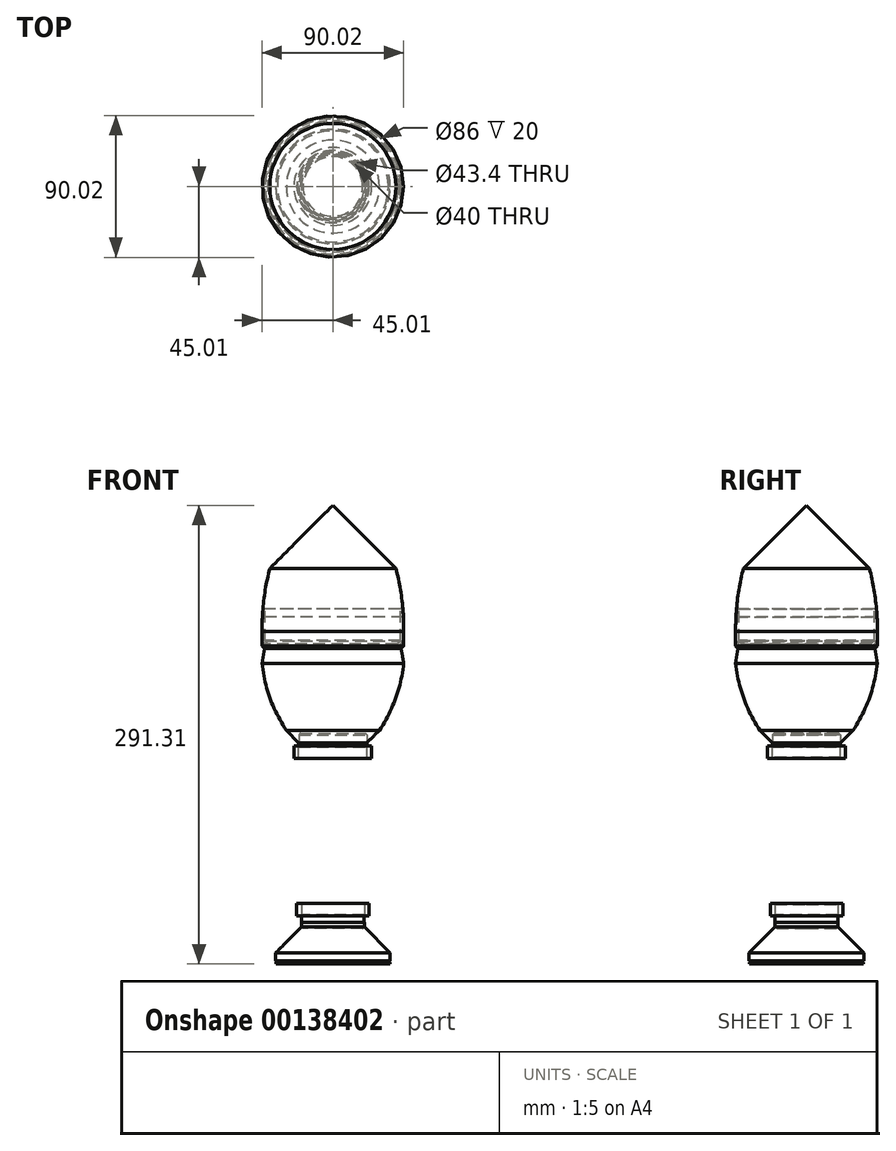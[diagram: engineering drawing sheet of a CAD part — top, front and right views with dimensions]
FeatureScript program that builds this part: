
annotation { "Feature Type Name" : "Feature", "Feature Type Description" : "" }
export const myFeature = defineFeature(function(context is Context, id is Id, definition is map)
    precondition{}
    {
        {
            var Q0;
            Q0=qCreatedBy(makeId("Front.planeOp"),FACE);
            var sketch = newSketch(context, id + "F0", { "sketchPlane" : qUnion([Q0])});
            skLineSegment(sketch, "E0", {"start": v(0, 155.81) * mm, "end": v(0, -136.19) * mm});
            skSolve(sketch);
        }
        {
            var Q0;
            Q0=qCreatedBy(makeId("Front.planeOp"),FACE);
            var sketch = newSketch(context, id + "F1", { "sketchPlane" : qUnion([Q0])});
            skLineSegment(sketch, "E1", {"start": v(0, 152.81) * mm, "end": v(40, 112.81) * mm});
            skPoint(sketch, "E2", {"position": v(44, 112.81) * mm});
            skLineSegment(sketch, "E3", {"start": v(40, 112.81) * mm, "end": v(40, 72.81) * mm});
            skLineSegment(sketch, "E4", {"start": v(40, 72.81) * mm, "end": v(0, 72.81) * mm});
            skLineSegment(sketch, "E5", {"start": v(0, 152.81) * mm, "end": v(0, 72.81) * mm});
            skArc(sketch, "E6", {"start": v(45, 72.81) * mm, "mid": v(43.83, 92.98) * mm, "end": v(40, 112.81) * mm});
            skLineSegment(sketch, "E7", {"start": v(45, 72.81) * mm, "end": v(40, 72.81) * mm});
            skSolve(sketch);
        }
        {
            var Q0;
            Q0 = qSketchRegion(id + "F1", true);
            var Q1;
            Q1=sQuery(id+"F0.wireOp",EDGE,"E0");
            revolve(context, id + "F2", {"surfaceOperationType" : NewSurfaceOperationType.NEW, "entities" : qUnion([Q0]), "axis" : qUnion([Q1]), "revolveType" : RevolveType.FULL});
        }
        {
            var Q0;
            Q0=qCreatedBy(makeId("Front.planeOp"),FACE);
            var sketch = newSketch(context, id + "F3", { "sketchPlane" : qUnion([Q0])});
            skLineSegment(sketch, "E8.bottom", {"start": v(30.98, 64.81) * mm, "end": v(43.2, 64.81) * mm});
            skLineSegment(sketch, "E8.top", {"start": v(0, 63.21) * mm, "end": v(41.6, 63.21) * mm});
            skLineSegment(sketch, "E8.left", {"start": v(0, 64.81) * mm, "end": v(0, 63.21) * mm});
            skLineSegment(sketch, "E8.right", {"start": v(44.6, 64.81) * mm, "end": v(44.6, 63.21) * mm});
            skLineSegment(sketch, "E9", {"start": v(44.6, 64.81) * mm, "end": v(44.6, 86.81) * mm});
            skLineSegment(sketch, "E10", {"start": v(44.07, 86.81) * mm, "end": v(43, 86.81) * mm});
            skLineSegment(sketch, "E11", {"start": v(43, 86.81) * mm, "end": v(43, 66.81) * mm});
            skLineSegment(sketch, "E12", {"start": v(30.98, 64.81) * mm, "end": v(30.98, 63.21) * mm});
            skLineSegment(sketch, "E13", {"start": v(43, 66.81) * mm, "end": v(41, 64.81) * mm});
            skPoint(sketch, "E14.orphan", {"position": v(43, 64.81) * mm});
            skLineSegment(sketch, "E15", {"start": v(44.6, 66.21) * mm, "end": v(41.6, 63.21) * mm});
            skLineSegment(sketch, "E16", {"start": v(0, 64.81) * mm, "end": v(30.98, 64.81) * mm});
            skLineSegment(sketch, "E17", {"start": v(44.07, 86.81) * mm, "end": v(44.6, 81.81) * mm});
            skSolve(sketch);
        }
        {
            var Q0;
            Q0 = qSketchRegion(id + "F3", true);
            var Q1;
            Q1=sQuery(id+"F3.wireOp",EDGE,"E8.left");
            revolve(context, id + "F4", {"surfaceOperationType" : NewSurfaceOperationType.NEW, "entities" : qUnion([Q0]), "axis" : qUnion([Q1]), "revolveType" : RevolveType.FULL});
        }
        {
            var Q0;
            Q0=qCreatedBy(makeId("Front.planeOp"),FACE);
            var sketch = newSketch(context, id + "F5", { "sketchPlane" : qUnion([Q0])});
            skLineSegment(sketch, "E18", {"start": v(0, 72.92) * mm, "end": v(45, 72.92) * mm});
            skLineSegment(sketch, "E19", {"start": v(0, 0) * mm, "end": v(21.7, 0) * mm});
            skLineSegment(sketch, "E20", {"start": v(0, 72.92) * mm, "end": v(0, 0) * mm});
            skArc(sketch, "E21", {"start": v(22, 0) * mm, "mid": v(37.53, 24.39) * mm, "end": v(45, 52.32) * mm});
            skLineSegment(sketch, "E22", {"start": v(45, 72.92) * mm, "end": v(45, 63.41) * mm});
            skLineSegment(sketch, "E23", {"start": v(45, 63.41) * mm, "end": v(43.36, 61.78) * mm});
            skLineSegment(sketch, "E24", {"start": v(43.36, 61.78) * mm, "end": v(45, 52.32) * mm});
            skLineSegment(sketch, "E25", {"start": v(21.7, 0) * mm, "end": v(21.7, 2) * mm});
            skLineSegment(sketch, "E26", {"start": v(21.7, 2) * mm, "end": v(29.57, 9.87) * mm});
            skSolve(sketch);
        }
        {
            var Q0;
            Q0 = qSketchRegion(id + "F5", true);
            var Q1;
            Q1=sQuery(id+"F5.wireOp",EDGE,"E20");
            revolve(context, id + "F6", {"surfaceOperationType" : NewSurfaceOperationType.NEW, "entities" : qUnion([Q0]), "axis" : qUnion([Q1]), "revolveType" : RevolveType.FULL});
        }
        {
            var Q0;
            Q0=makeQuery(id+"F6.opRevolve","SWEPT_FACE",FACE,{"disambiguationData":[OSD([sQuery(id+"F5.wireOp",EDGE,"E19")])]});
            var sketch = newSketch(context, id + "F7", { "sketchPlane" : qUnion([Q0])});
            skCircle(sketch, "E27", {"center": v(0, 0) * mm, "radius": 21.6 * mm});
            skSolve(sketch);
        }
        {
            var Q0;
            Q0 = qSketchRegion(id + "F7", true);
            extrude(context, id + "F8", {"entities" : qUnion([Q0]), "oppositeDirection" : true, "depth" : 8 * mm, "offsetDistance" : 25 * mm});
        }
        {
            var Q0;
            Q0=qCreatedBy(makeId("Front.planeOp"),FACE);
            var sketch = newSketch(context, id + "F9", { "sketchPlane" : qUnion([Q0])});
            skLineSegment(sketch, "E28", {"start": v(0, -112) * mm, "end": v(20, -112) * mm});
            skLineSegment(sketch, "E29", {"start": v(36.4, -136.5) * mm, "end": v(0, -136.5) * mm});
            skLineSegment(sketch, "E30", {"start": v(0, -136.5) * mm, "end": v(0, -112) * mm});
            skLineSegment(sketch, "E31", {"start": v(20, -112) * mm, "end": v(20, -115.1) * mm});
            skLineSegment(sketch, "E32", {"start": v(20, -115.1) * mm, "end": v(36.4, -131.5) * mm});
            skLineSegment(sketch, "E33", {"start": v(36.4, -131.5) * mm, "end": v(36.4, -136.5) * mm});
            skSolve(sketch);
        }
        {
            var Q0;
            Q0 = qSketchRegion(id + "F9", true);
            var Q1;
            Q1=sQuery(id+"F9.wireOp",EDGE,"E30");
            revolve(context, id + "F10", {"surfaceOperationType" : NewSurfaceOperationType.NEW, "entities" : qUnion([Q0]), "axis" : qUnion([Q1]), "revolveType" : RevolveType.FULL});
        }
        {
            var Q0;
            Q0=makeQuery(id+"F10.opRevolve","SWEPT_FACE",FACE,{"disambiguationData":[OSD([sQuery(id+"F9.wireOp",EDGE,"E28")])]});
            var sketch = newSketch(context, id + "F11", { "sketchPlane" : qUnion([Q0])});
            skCircle(sketch, "E34", {"center": v(0, 0) * mm, "radius": 19.9 * mm});
            skSolve(sketch);
        }
        {
            var Q0;
            Q0 = qSketchRegion(id + "F11", true);
            extrude(context, id + "F12", {"entities" : qUnion([Q0]), "oppositeDirection" : true, "depth" : 8 * mm, "offsetDistance" : 25 * mm, "symmetric" : true});
        }
        {
            var Q0;
            Q0=makeQuery(id+"F10.opRevolve","SWEPT_FACE",FACE,{"disambiguationData":[OSD([sQuery(id+"F9.wireOp",EDGE,"E29")])]});
            var sketch = newSketch(context, id + "F13", { "sketchPlane" : qUnion([Q0])});
            skCircle(sketch, "E35", {"center": v(0, 0) * mm, "radius": 36.2 * mm});
            skSolve(sketch);
        }
        {
            var Q0;
            Q0 = qSketchRegion(id + "F13", true);
            extrude(context, id + "F14", {"entities" : qUnion([Q0]), "depth" : 2 * mm, "offsetDistance" : 25 * mm});
        }
        {
            var Q0;
            Q0=makeQuery(id+"F8.opExtrude","CAP_FACE",FACE,{"disambiguationData":[OSD([sQuery(id+"F7.wireOp",EDGE,"E27")])],"isStart":false});
            var Q1;
            Q1=makeQuery(id+"F12.opExtrude","CAP_FACE",FACE,{"disambiguationData":[OSD([sQuery(id+"F11.wireOp",EDGE,"E34")])],"isStart":false});
            var Q2;
            Q2=makeQuery(id+"F14.opExtrude","CAP_FACE",FACE,{"disambiguationData":[OSD([sQuery(id+"F13.wireOp",EDGE,"E35")])],"isStart":true});
            chamfer(context, id + "F15", {"entities" : qUnion([Q0, Q1, Q2]), "width" : 1 * mm, "tangentPropagation" : true});
        }
        {
            var Q0;
            Q0=makeQuery(id+"F12.opExtrude","CAP_FACE",FACE,{"disambiguationData":[OSD([sQuery(id+"F11.wireOp",EDGE,"E34")])],"isStart":true});
            var sketch = newSketch(context, id + "F16", { "sketchPlane" : qUnion([Q0])});
            skCircle(sketch, "E36", {"center": v(0, 0) * mm, "radius": 20 * mm});
            skCircle(sketch, "E37", {"center": v(0, 0) * mm, "radius": 23 * mm});
            skSolve(sketch);
        }
        {
            var Q0;
            Q0 = qSketchRegion(id + "F16", true);
            extrude(context, id + "F17", {"entities" : qUnion([Q0]), "depth" : 8 * mm, "offsetDistance" : 25 * mm});
        }
        {
            var Q0;
            Q0=makeQuery(id+"F8.opExtrude","CAP_FACE",FACE,{"disambiguationData":[OSD([sQuery(id+"F7.wireOp",EDGE,"E27")])],"isStart":true});
            var sketch = newSketch(context, id + "F18", { "sketchPlane" : qUnion([Q0])});
            skCircle(sketch, "E38", {"center": v(0, 0) * mm, "radius": 21.7 * mm});
            skCircle(sketch, "E39", {"center": v(0, 0) * mm, "radius": 24.7 * mm});
            skSolve(sketch);
        }
        {
            var Q0;
            Q0 = qSketchRegion(id + "F18", true);
            extrude(context, id + "F19", {"entities" : qUnion([Q0]), "depth" : 8 * mm, "offsetDistance" : 25 * mm});
        }
        {
            var Q0;
            Q0=makeQuery(id+"F17.opExtrude","CAP_EDGE",EDGE,{"disambiguationData":[OSD([sQuery(id+"F16.wireOp",EDGE,"E36")])],"isStart":false});
            var Q1;
            Q1=makeQuery(id+"F17.opExtrude","CAP_EDGE",EDGE,{"disambiguationData":[OSD([sQuery(id+"F16.wireOp",EDGE,"E36")])],"isStart":true});
            var Q2;
            Q2=makeQuery(id+"F19.opExtrude","CAP_EDGE",EDGE,{"disambiguationData":[OSD([sQuery(id+"F18.wireOp",EDGE,"E38")])],"isStart":false});
            var Q3;
            Q3=makeQuery(id+"F19.opExtrude","CAP_EDGE",EDGE,{"disambiguationData":[OSD([sQuery(id+"F18.wireOp",EDGE,"E38")])],"isStart":true});
            chamfer(context, id + "F20", {"entities" : qUnion([Q0, Q1, Q2, Q3]), "width" : 0.8 * mm, "tangentPropagation" : true});
        }
    });
